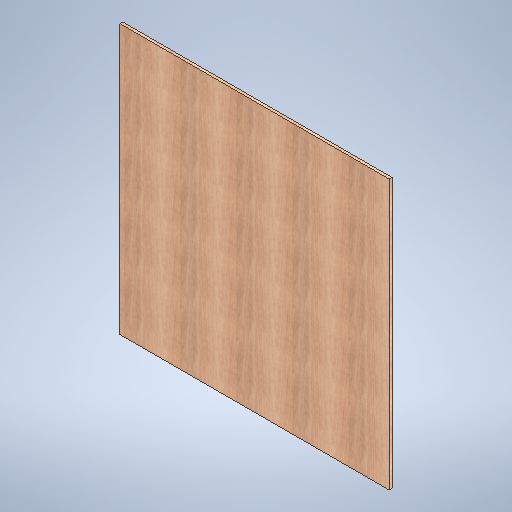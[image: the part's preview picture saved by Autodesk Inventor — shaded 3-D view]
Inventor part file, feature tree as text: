
AUTODESK INVENTOR PART (.ipt)
format: ipt  version: 2025 (Build 290162010, 162A)  size: 392,192 bytes
history: native  units: in
note: dims shown in document units (in); Inventor stores cm internally (conversion verified against a paired STEP export)
features: extrude x1, sketch x1
ambient origin geometry x8: Origin, YZ Plane, XZ Plane, XY Plane, X Axis, Y Axis, Z Axis, Center Point
bodies: Solid1 (feature_tree)
feature tree (2):
  extrude  "Extrusion1"  Depth=48.0in
  sketch  "Sketch1"  dims[d2=48.0in d3=48.0in d4=0.5in d5=0.0in]
